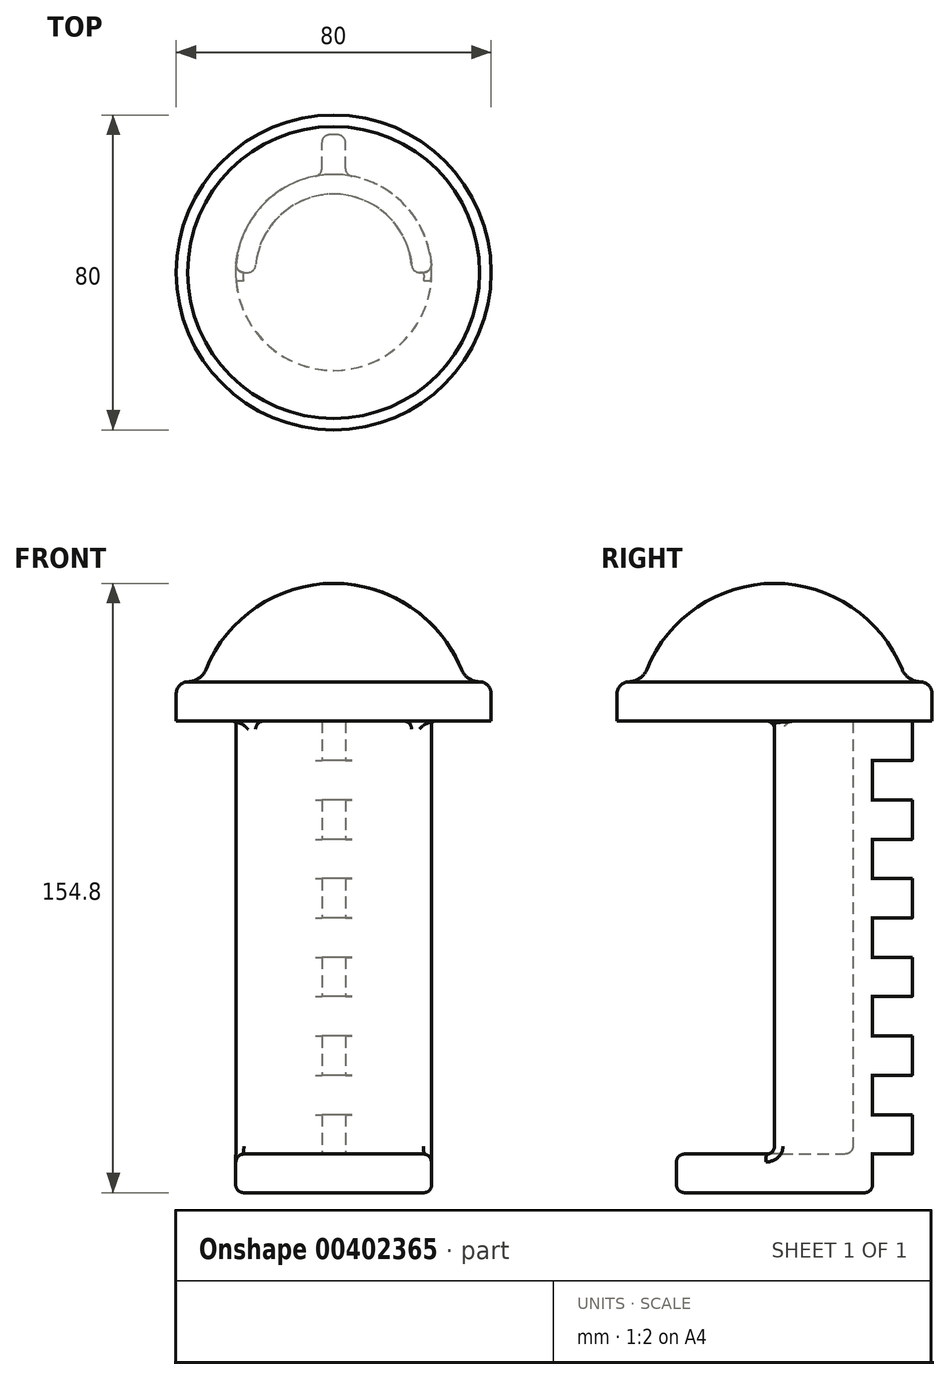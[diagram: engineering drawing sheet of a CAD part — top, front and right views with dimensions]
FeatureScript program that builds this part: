
annotation { "Feature Type Name" : "Feature", "Feature Type Description" : "" }
export const myFeature = defineFeature(function(context is Context, id is Id, definition is map)
    precondition{}
    {
        {
            var Q0;
            Q0=qCreatedBy(makeId("Top.planeOp"),FACE);
            var sketch = newSketch(context, id + "F0", { "sketchPlane" : qUnion([Q0])});
            skCircle(sketch, "E0", {"center": v(0, 0) * mm, "radius": 24.9 * mm});
            skSolve(sketch);
        }
        {
            var Q0;
            Q0=makeQuery(id+"F0.imprint","IMPRINT",FACE,{"disambiguationData":[TD([[makeQuery(id+"F0.imprint","IMPRINT",EDGE,{"derivedFrom":sQuery(id+"F0.wireOp",EDGE,"E0")}),1.0]])]});
            extrude(context, id + "F1", {"entities" : qUnion([Q0]), "depth" : 9.8 * mm});
        }
        {
            var Q0;
            Q0=makeQuery(id+"F1.opExtrude","CAP_FACE",FACE,{"disambiguationData":[OSD([sQuery(id+"F0.wireOp",EDGE,"E0")])],"isStart":false});
            var sketch = newSketch(context, id + "F2", { "sketchPlane" : qUnion([Q0])});
            skArc(sketch, "E1", {"start": v(-4.63, 24.47) * mm, "mid": v(-24.8, -2.32) * mm, "end": v(0, -24.9) * mm});
            skPoint(sketch, "E1.first.point", {"position": v(-24.85, 1.59) * mm});
            skPoint(sketch, "E1.second.point", {"position": v(24.55, 4.16) * mm});
            skPoint(sketch, "E1.third.point", {"position": v(0, -24.9) * mm});
            skArc(sketch, "E2", {"start": v(1.06, 34.98) * mm, "mid": v(0, 35) * mm, "end": v(-1.06, 34.98) * mm});
            skLineSegment(sketch, "E3", {"start": v(0, 0) * mm, "end": v(0, 45.08) * mm, "construction": true});
            skLineSegment(sketch, "E4", {"start": v(-3, 26.43) * mm, "end": v(-3, 32.98) * mm});
            skLineSegment(sketch, "E5", {"start": v(3, 26.43) * mm, "end": v(3, 32.98) * mm});
            skPoint(sketch, "E6.orphan", {"position": v(-3, 0) * mm});
            skPoint(sketch, "E7.orphan", {"position": v(3, 0) * mm});
            skPoint(sketch, "E8.visualSharp", {"position": v(-3, 24.72) * mm});
            skArc(sketch, "E8.filletArc", {"start": v(-4.63, 24.47) * mm, "mid": v(-3.46, 25.16) * mm, "end": v(-3, 26.43) * mm});
            skPoint(sketch, "E9.visualSharp", {"position": v(-3, 34.87) * mm});
            skArc(sketch, "E9.filletArc", {"start": v(-1.06, 34.98) * mm, "mid": v(-2.44, 34.38) * mm, "end": v(-3, 32.98) * mm});
            skPoint(sketch, "E10.visualSharp", {"position": v(3, 34.87) * mm});
            skArc(sketch, "E10.filletArc", {"start": v(3, 32.98) * mm, "mid": v(2.44, 34.38) * mm, "end": v(1.06, 34.98) * mm});
            skPoint(sketch, "E11.visualSharp", {"position": v(3, 24.72) * mm});
            skArc(sketch, "E11.filletArc", {"start": v(3, 26.43) * mm, "mid": v(3.46, 25.16) * mm, "end": v(4.63, 24.47) * mm});
            skArc(sketch, "E12", {"start": v(19.9, 0) * mm, "mid": v(0, 19.9) * mm, "end": v(-19.9, 0) * mm});
            skLineSegment(sketch, "E13", {"start": v(-24.9, 0) * mm, "end": v(-19.9, 0) * mm});
            skLineSegment(sketch, "E14.trimOffspring", {"start": v(19.9, 0) * mm, "end": v(24.9, 0) * mm});
            skArc(sketch, "E15.trimOffspring", {"start": v(24.9, 0) * mm, "mid": v(19.17, 15.89) * mm, "end": v(4.63, 24.47) * mm});
            skSolve(sketch);
        }
        {
            var Q0;
            Q0 = qSketchRegion(id + "F2", true);
            extrude(context, id + "F3", {"entities" : qUnion([Q0]), "operationType" : NewBodyOperationType.ADD, "depth" : 10 * mm});
        }
        {
            var Q0;
            Q0=makeQuery(id+"F3.opExtrude","CAP_FACE",FACE,{"disambiguationData":[OSD([sQuery(id+"F2.wireOp",EDGE,"E1"),sQuery(id+"F2.wireOp",EDGE,"E2"),sQuery(id+"F2.wireOp",EDGE,"E4"),sQuery(id+"F2.wireOp",EDGE,"E5"),sQuery(id+"F2.wireOp",EDGE,"E8.filletArc"),sQuery(id+"F2.wireOp",EDGE,"E9.filletArc"),sQuery(id+"F2.wireOp",EDGE,"E10.filletArc"),sQuery(id+"F2.wireOp",EDGE,"E11.filletArc"),sQuery(id+"F2.wireOp",EDGE,"E12"),sQuery(id+"F2.wireOp",EDGE,"E13"),sQuery(id+"F2.wireOp",EDGE,"E14.trimOffspring"),sQuery(id+"F2.wireOp",EDGE,"E15.trimOffspring")])],"isStart":false});
            var sketch = newSketch(context, id + "F4", { "sketchPlane" : qUnion([Q0])});
            skArc(sketch, "E16", {"start": v(19.9, 0) * mm, "mid": v(0, 19.9) * mm, "end": v(-19.9, 0) * mm});
            skArc(sketch, "E17", {"start": v(24.9, 0) * mm, "mid": v(0, 24.9) * mm, "end": v(-24.9, 0) * mm});
            skLineSegment(sketch, "E18", {"start": v(24.9, 0) * mm, "end": v(19.9, 0) * mm});
            skLineSegment(sketch, "E19.trimOffspring", {"start": v(-19.9, 0) * mm, "end": v(-24.9, 0) * mm});
            skSolve(sketch);
        }
        {
            var Q0;
            Q0=makeQuery(id+"F4.imprint","IMPRINT",FACE,{"disambiguationData":[TD([[makeQuery(id+"F4.imprint","IMPRINT",EDGE,{"derivedFrom":sQuery(id+"F4.wireOp",EDGE,"E16")}),-1.0]])]});
            extrude(context, id + "F5", {"entities" : qUnion([Q0]), "operationType" : NewBodyOperationType.ADD, "depth" : 10 * mm});
        }
        {
            var Q0;
            Q0=makeQuery(id+"F5.opExtrude","CAP_FACE",FACE,{"disambiguationData":[OSD([sQuery(id+"F4.wireOp",EDGE,"E16"),sQuery(id+"F4.wireOp",EDGE,"E17"),sQuery(id+"F4.wireOp",EDGE,"E18"),sQuery(id+"F4.wireOp",EDGE,"E19.trimOffspring")])],"isStart":false});
            var sketch = newSketch(context, id + "F6", { "sketchPlane" : qUnion([Q0])});
            skArc(sketch, "E20", {"start": v(19.9, 0) * mm, "mid": v(0, 19.9) * mm, "end": v(-19.9, 0) * mm});
            skPoint(sketch, "E20.first.point", {"position": v(-18.97, 6.02) * mm});
            skPoint(sketch, "E20.second.point", {"position": v(3.48, 19.6) * mm});
            skPoint(sketch, "E20.third.point", {"position": v(17.46, 9.55) * mm});
            skArc(sketch, "E21", {"start": v(24.9, 0) * mm, "mid": v(19.17, 15.89) * mm, "end": v(4.63, 24.47) * mm});
            skLineSegment(sketch, "E22", {"start": v(24.9, 0) * mm, "end": v(19.9, 0) * mm});
            skArc(sketch, "E23", {"start": v(1.06, 34.98) * mm, "mid": v(0, 35) * mm, "end": v(-1.06, 34.98) * mm});
            skLineSegment(sketch, "E24", {"start": v(-3, 26.43) * mm, "end": v(-3, 32.98) * mm});
            skLineSegment(sketch, "E25", {"start": v(3, 26.43) * mm, "end": v(3, 32.98) * mm});
            skLineSegment(sketch, "E26", {"start": v(0, 0) * mm, "end": v(0, 56.77) * mm, "construction": true});
            skLineSegment(sketch, "E27.trimOffspring", {"start": v(-19.9, 0) * mm, "end": v(-24.9, 0) * mm});
            skArc(sketch, "E28.trimOffspring", {"start": v(-4.63, 24.47) * mm, "mid": v(-19.17, 15.89) * mm, "end": v(-24.9, 0) * mm});
            skArc(sketch, "E29.filletArc", {"start": v(3, 26.43) * mm, "mid": v(3.46, 25.16) * mm, "end": v(4.63, 24.47) * mm});
            skPoint(sketch, "E30.visualSharp", {"position": v(3, 34.87) * mm});
            skArc(sketch, "E30.filletArc", {"start": v(3, 32.98) * mm, "mid": v(2.44, 34.38) * mm, "end": v(1.06, 34.98) * mm});
            skPoint(sketch, "E31.visualSharp", {"position": v(-3, 34.87) * mm});
            skArc(sketch, "E31.filletArc", {"start": v(-1.06, 34.98) * mm, "mid": v(-2.44, 34.38) * mm, "end": v(-3, 32.98) * mm});
            skArc(sketch, "E32.filletArc", {"start": v(-4.63, 24.47) * mm, "mid": v(-3.46, 25.16) * mm, "end": v(-3, 26.43) * mm});
            skSolve(sketch);
        }
        {
            var Q0;
            Q0 = qSketchRegion(id + "F6", true);
            extrude(context, id + "F7", {"entities" : qUnion([Q0]), "operationType" : NewBodyOperationType.ADD, "depth" : 10 * mm});
        }
        {
            var Q0;
            Q0=makeQuery(id+"F7.opExtrude","CAP_FACE",FACE,{"disambiguationData":[OSD([sQuery(id+"F6.wireOp",EDGE,"E20"),sQuery(id+"F6.wireOp",EDGE,"E21"),sQuery(id+"F6.wireOp",EDGE,"E22"),sQuery(id+"F6.wireOp",EDGE,"E23"),sQuery(id+"F6.wireOp",EDGE,"E24"),sQuery(id+"F6.wireOp",EDGE,"E25"),sQuery(id+"F6.wireOp",EDGE,"E27.trimOffspring"),sQuery(id+"F6.wireOp",EDGE,"E28.trimOffspring"),sQuery(id+"F6.wireOp",EDGE,"E29.filletArc"),sQuery(id+"F6.wireOp",EDGE,"E30.filletArc"),sQuery(id+"F6.wireOp",EDGE,"E31.filletArc"),sQuery(id+"F6.wireOp",EDGE,"E32.filletArc")])],"isStart":false});
            var sketch = newSketch(context, id + "F8", { "sketchPlane" : qUnion([Q0])});
            skArc(sketch, "E33", {"start": v(19.9, 0) * mm, "mid": v(0, 19.9) * mm, "end": v(-19.9, 0) * mm});
            skPoint(sketch, "E33.first.point", {"position": v(-19.37, 4.56) * mm});
            skPoint(sketch, "E33.second.point", {"position": v(0, 19.9) * mm});
            skPoint(sketch, "E33.third.point", {"position": v(12.83, 15.21) * mm});
            skArc(sketch, "E34", {"start": v(24.9, 0) * mm, "mid": v(0, 24.9) * mm, "end": v(-24.9, 0) * mm});
            skLineSegment(sketch, "E35", {"start": v(-24.9, 0) * mm, "end": v(-19.9, 0) * mm});
            skLineSegment(sketch, "E36.trimOffspring", {"start": v(19.9, 0) * mm, "end": v(24.9, 0) * mm});
            skSolve(sketch);
        }
        {
            var Q0;
            Q0=makeQuery(id+"F8.imprint","IMPRINT",FACE,{"disambiguationData":[TD([[makeQuery(id+"F8.imprint","IMPRINT",EDGE,{"derivedFrom":sQuery(id+"F8.wireOp",EDGE,"E33")}),-1.0]])]});
            extrude(context, id + "F9", {"entities" : qUnion([Q0]), "operationType" : NewBodyOperationType.ADD, "depth" : 10 * mm});
        }
        {
            var Q0;
            Q0=makeQuery(id+"F9.opExtrude","CAP_FACE",FACE,{"disambiguationData":[OSD([sQuery(id+"F8.wireOp",EDGE,"E33"),sQuery(id+"F8.wireOp",EDGE,"E34"),sQuery(id+"F8.wireOp",EDGE,"E35"),sQuery(id+"F8.wireOp",EDGE,"E36.trimOffspring")])],"isStart":false});
            var sketch = newSketch(context, id + "F10", { "sketchPlane" : qUnion([Q0])});
            skArc(sketch, "E37", {"start": v(19.9, 0) * mm, "mid": v(0, 19.9) * mm, "end": v(-19.9, 0) * mm});
            skPoint(sketch, "E37.first.point", {"position": v(-19.75, 2.44) * mm});
            skPoint(sketch, "E37.second.point", {"position": v(-1.95, 19.8) * mm});
            skPoint(sketch, "E37.third.point", {"position": v(19.22, 5.17) * mm});
            skArc(sketch, "E38", {"start": v(24.9, 0) * mm, "mid": v(19.17, 15.89) * mm, "end": v(4.63, 24.47) * mm});
            skPoint(sketch, "E38.first.point", {"position": v(-19.14, 15.92) * mm});
            skPoint(sketch, "E38.second.point", {"position": v(8.15, 23.53) * mm});
            skPoint(sketch, "E38.third.point", {"position": v(24.48, 4.54) * mm});
            skArc(sketch, "E39", {"start": v(1.06, 34.98) * mm, "mid": v(0, 35) * mm, "end": v(-1.06, 34.98) * mm});
            skLineSegment(sketch, "E40", {"start": v(24.9, 0) * mm, "end": v(19.9, 0) * mm});
            skLineSegment(sketch, "E41", {"start": v(0, 0) * mm, "end": v(0, 39.15) * mm, "construction": true});
            skLineSegment(sketch, "E42", {"start": v(-3, 26.43) * mm, "end": v(-3, 32.98) * mm});
            skLineSegment(sketch, "E43", {"start": v(3, 26.43) * mm, "end": v(3, 32.98) * mm});
            skArc(sketch, "E44.trimOffspring", {"start": v(-4.63, 24.47) * mm, "mid": v(-19.17, 15.89) * mm, "end": v(-24.9, 0) * mm});
            skLineSegment(sketch, "E45.trimOffspring", {"start": v(-19.9, 0) * mm, "end": v(-24.9, 0) * mm});
            skPoint(sketch, "E46.visualSharp", {"position": v(-3, 24.72) * mm});
            skArc(sketch, "E46.filletArc", {"start": v(-4.63, 24.47) * mm, "mid": v(-3.46, 25.16) * mm, "end": v(-3, 26.43) * mm});
            skPoint(sketch, "E47.visualSharp", {"position": v(3, 24.72) * mm});
            skArc(sketch, "E47.filletArc", {"start": v(3, 26.43) * mm, "mid": v(3.46, 25.16) * mm, "end": v(4.63, 24.47) * mm});
            skPoint(sketch, "E48.visualSharp", {"position": v(-3, 34.87) * mm});
            skArc(sketch, "E48.filletArc", {"start": v(-1.06, 34.98) * mm, "mid": v(-2.44, 34.38) * mm, "end": v(-3, 32.98) * mm});
            skPoint(sketch, "E49.visualSharp", {"position": v(3, 34.87) * mm});
            skArc(sketch, "E49.filletArc", {"start": v(3, 32.98) * mm, "mid": v(2.44, 34.38) * mm, "end": v(1.06, 34.98) * mm});
            skSolve(sketch);
        }
        {
            var Q0;
            Q0 = qSketchRegion(id + "F10", true);
            extrude(context, id + "F11", {"entities" : qUnion([Q0]), "operationType" : NewBodyOperationType.ADD, "depth" : 10 * mm});
        }
        {
            var Q0;
            Q0=makeQuery(id+"F11.opExtrude","CAP_FACE",FACE,{"disambiguationData":[OSD([sQuery(id+"F10.wireOp",EDGE,"E37"),sQuery(id+"F10.wireOp",EDGE,"E38"),sQuery(id+"F10.wireOp",EDGE,"E39"),sQuery(id+"F10.wireOp",EDGE,"E40"),sQuery(id+"F10.wireOp",EDGE,"E42"),sQuery(id+"F10.wireOp",EDGE,"E43"),sQuery(id+"F10.wireOp",EDGE,"E44.trimOffspring"),sQuery(id+"F10.wireOp",EDGE,"E45.trimOffspring"),sQuery(id+"F10.wireOp",EDGE,"E46.filletArc"),sQuery(id+"F10.wireOp",EDGE,"E47.filletArc"),sQuery(id+"F10.wireOp",EDGE,"E48.filletArc"),sQuery(id+"F10.wireOp",EDGE,"E49.filletArc")])],"isStart":false});
            var sketch = newSketch(context, id + "F12", { "sketchPlane" : qUnion([Q0])});
            skArc(sketch, "E50", {"start": v(19.9, 0) * mm, "mid": v(0, 19.9) * mm, "end": v(-19.9, 0) * mm});
            skPoint(sketch, "E50.first.point", {"position": v(-19.35, 4.65) * mm});
            skPoint(sketch, "E50.second.point", {"position": v(-7.36, 18.49) * mm});
            skPoint(sketch, "E50.third.point", {"position": v(18.26, 7.9) * mm});
            skArc(sketch, "E51", {"start": v(24.9, 0) * mm, "mid": v(0, 24.9) * mm, "end": v(-24.9, 0) * mm});
            skLineSegment(sketch, "E52", {"start": v(-24.9, 0) * mm, "end": v(-19.9, 0) * mm});
            skLineSegment(sketch, "E53.trimOffspring", {"start": v(19.9, 0) * mm, "end": v(24.9, 0) * mm});
            skSolve(sketch);
        }
        {
            var Q0;
            Q0 = qSketchRegion(id + "F12", true);
            extrude(context, id + "F13", {"entities" : qUnion([Q0]), "operationType" : NewBodyOperationType.ADD, "depth" : 10 * mm});
        }
        {
            var Q0;
            Q0=makeQuery(id+"F13.opExtrude","CAP_FACE",FACE,{"disambiguationData":[OSD([sQuery(id+"F12.wireOp",EDGE,"E50"),sQuery(id+"F12.wireOp",EDGE,"E51"),sQuery(id+"F12.wireOp",EDGE,"E52"),sQuery(id+"F12.wireOp",EDGE,"E53.trimOffspring")])],"isStart":false});
            var sketch = newSketch(context, id + "F14", { "sketchPlane" : qUnion([Q0])});
            skArc(sketch, "E54", {"start": v(19.9, 0) * mm, "mid": v(0, 19.9) * mm, "end": v(-19.9, 0) * mm});
            skPoint(sketch, "E54.first.point", {"position": v(16.62, 10.94) * mm});
            skPoint(sketch, "E54.second.point", {"position": v(3.42, 19.6) * mm});
            skPoint(sketch, "E54.third.point", {"position": v(-17.92, 8.65) * mm});
            skArc(sketch, "E55", {"start": v(24.9, 0) * mm, "mid": v(19.17, 15.89) * mm, "end": v(4.63, 24.47) * mm});
            skArc(sketch, "E56", {"start": v(1.06, 34.98) * mm, "mid": v(0, 35) * mm, "end": v(-1.06, 34.98) * mm});
            skLineSegment(sketch, "E57", {"start": v(-24.9, 0) * mm, "end": v(-19.9, 0) * mm});
            skLineSegment(sketch, "E58", {"start": v(0, 0) * mm, "end": v(0, 36.44) * mm, "construction": true});
            skLineSegment(sketch, "E59", {"start": v(-3, 26.43) * mm, "end": v(-3, 32.98) * mm});
            skLineSegment(sketch, "E60", {"start": v(3, 26.43) * mm, "end": v(3, 32.98) * mm});
            skArc(sketch, "E61.trimOffspring", {"start": v(-4.63, 24.47) * mm, "mid": v(-19.17, 15.89) * mm, "end": v(-24.9, 0) * mm});
            skLineSegment(sketch, "E62.trimOffspring", {"start": v(19.9, 0) * mm, "end": v(24.9, 0) * mm});
            skPoint(sketch, "E63.visualSharp", {"position": v(-3, 24.72) * mm});
            skArc(sketch, "E63.filletArc", {"start": v(-4.63, 24.47) * mm, "mid": v(-3.46, 25.16) * mm, "end": v(-3, 26.43) * mm});
            skPoint(sketch, "E64.visualSharp", {"position": v(-3, 34.87) * mm});
            skArc(sketch, "E64.filletArc", {"start": v(-1.06, 34.98) * mm, "mid": v(-2.44, 34.38) * mm, "end": v(-3, 32.98) * mm});
            skPoint(sketch, "E65.visualSharp", {"position": v(3, 34.87) * mm});
            skArc(sketch, "E65.filletArc", {"start": v(3, 32.98) * mm, "mid": v(2.44, 34.38) * mm, "end": v(1.06, 34.98) * mm});
            skPoint(sketch, "E66.visualSharp", {"position": v(3, 24.72) * mm});
            skArc(sketch, "E66.filletArc", {"start": v(3, 26.43) * mm, "mid": v(3.46, 25.16) * mm, "end": v(4.63, 24.47) * mm});
            skSolve(sketch);
        }
        {
            var Q0;
            Q0 = qSketchRegion(id + "F14", true);
            extrude(context, id + "F15", {"entities" : qUnion([Q0]), "operationType" : NewBodyOperationType.ADD, "depth" : 10 * mm});
        }
        {
            var Q0;
            Q0=makeQuery(id+"F15.opExtrude","CAP_FACE",FACE,{"disambiguationData":[OSD([sQuery(id+"F14.wireOp",EDGE,"E54"),sQuery(id+"F14.wireOp",EDGE,"E55"),sQuery(id+"F14.wireOp",EDGE,"E56"),sQuery(id+"F14.wireOp",EDGE,"E57"),sQuery(id+"F14.wireOp",EDGE,"E59"),sQuery(id+"F14.wireOp",EDGE,"E60"),sQuery(id+"F14.wireOp",EDGE,"E61.trimOffspring"),sQuery(id+"F14.wireOp",EDGE,"E62.trimOffspring"),sQuery(id+"F14.wireOp",EDGE,"E63.filletArc"),sQuery(id+"F14.wireOp",EDGE,"E64.filletArc"),sQuery(id+"F14.wireOp",EDGE,"E65.filletArc"),sQuery(id+"F14.wireOp",EDGE,"E66.filletArc")])],"isStart":false});
            var sketch = newSketch(context, id + "F16", { "sketchPlane" : qUnion([Q0])});
            skArc(sketch, "E67", {"start": v(19.9, 0) * mm, "mid": v(0, 19.9) * mm, "end": v(-19.9, 0) * mm});
            skPoint(sketch, "E67.first.point", {"position": v(-19.61, 3.37) * mm});
            skPoint(sketch, "E67.second.point", {"position": v(-4.07, 19.48) * mm});
            skPoint(sketch, "E67.third.point", {"position": v(18.8, 6.54) * mm});
            skArc(sketch, "E68", {"start": v(24.9, 0) * mm, "mid": v(0, 24.9) * mm, "end": v(-24.9, 0) * mm});
            skLineSegment(sketch, "E69", {"start": v(-24.9, 0) * mm, "end": v(-19.9, 0) * mm});
            skLineSegment(sketch, "E70.trimOffspring", {"start": v(19.9, 0) * mm, "end": v(24.9, 0) * mm});
            skSolve(sketch);
        }
        {
            var Q0;
            Q0 = qSketchRegion(id + "F16", true);
            extrude(context, id + "F17", {"entities" : qUnion([Q0]), "operationType" : NewBodyOperationType.ADD, "depth" : 10 * mm});
        }
        {
            var Q0;
            Q0=makeQuery(id+"F17.opExtrude","CAP_FACE",FACE,{"disambiguationData":[OSD([sQuery(id+"F16.wireOp",EDGE,"E67"),sQuery(id+"F16.wireOp",EDGE,"E68"),sQuery(id+"F16.wireOp",EDGE,"E69"),sQuery(id+"F16.wireOp",EDGE,"E70.trimOffspring")])],"isStart":false});
            var sketch = newSketch(context, id + "F18", { "sketchPlane" : qUnion([Q0])});
            skArc(sketch, "E71", {"start": v(19.9, 0) * mm, "mid": v(0, 19.9) * mm, "end": v(-19.9, 0) * mm});
            skPoint(sketch, "E71.first.point", {"position": v(-19.39, 4.5) * mm});
            skPoint(sketch, "E71.second.point", {"position": v(-4.82, 19.3) * mm});
            skPoint(sketch, "E71.third.point", {"position": v(18.4, 7.6) * mm});
            skArc(sketch, "E72", {"start": v(-4.63, 24.47) * mm, "mid": v(-19.17, 15.89) * mm, "end": v(-24.9, 0) * mm});
            skArc(sketch, "E73", {"start": v(1.06, 34.98) * mm, "mid": v(0, 35) * mm, "end": v(-1.06, 34.98) * mm});
            skLineSegment(sketch, "E74", {"start": v(24.9, 0) * mm, "end": v(19.9, 0) * mm});
            skLineSegment(sketch, "E75", {"start": v(0, 0) * mm, "end": v(0, 36.8) * mm, "construction": true});
            skLineSegment(sketch, "E76.trimOffspring", {"start": v(3, 26.43) * mm, "end": v(3, 32.98) * mm});
            skLineSegment(sketch, "E77.trimOffspring", {"start": v(-3, 26.43) * mm, "end": v(-3, 32.98) * mm});
            skLineSegment(sketch, "E78.trimOffspring", {"start": v(-19.9, 0) * mm, "end": v(-24.9, 0) * mm});
            skArc(sketch, "E79.trimOffspring", {"start": v(24.9, 0) * mm, "mid": v(19.17, 15.89) * mm, "end": v(4.63, 24.47) * mm});
            skPoint(sketch, "E80.visualSharp", {"position": v(-3, 24.72) * mm});
            skArc(sketch, "E80.filletArc", {"start": v(-4.63, 24.47) * mm, "mid": v(-3.46, 25.16) * mm, "end": v(-3, 26.43) * mm});
            skPoint(sketch, "E81.visualSharp", {"position": v(-3, 34.87) * mm});
            skArc(sketch, "E81.filletArc", {"start": v(-1.06, 34.98) * mm, "mid": v(-2.44, 34.38) * mm, "end": v(-3, 32.98) * mm});
            skPoint(sketch, "E82.visualSharp", {"position": v(3, 34.87) * mm});
            skArc(sketch, "E82.filletArc", {"start": v(3, 32.98) * mm, "mid": v(2.44, 34.38) * mm, "end": v(1.06, 34.98) * mm});
            skPoint(sketch, "E83.visualSharp", {"position": v(3, 24.72) * mm});
            skArc(sketch, "E83.filletArc", {"start": v(3, 26.43) * mm, "mid": v(3.46, 25.16) * mm, "end": v(4.63, 24.47) * mm});
            skSolve(sketch);
        }
        {
            var Q0;
            Q0 = qSketchRegion(id + "F18", true);
            extrude(context, id + "F19", {"entities" : qUnion([Q0]), "operationType" : NewBodyOperationType.ADD, "depth" : 10 * mm});
        }
        {
            var Q0;
            Q0=makeQuery(id+"F19.opExtrude","CAP_FACE",FACE,{"disambiguationData":[OSD([sQuery(id+"F18.wireOp",EDGE,"E71"),sQuery(id+"F18.wireOp",EDGE,"E72"),sQuery(id+"F18.wireOp",EDGE,"E73"),sQuery(id+"F18.wireOp",EDGE,"E74"),sQuery(id+"F18.wireOp",EDGE,"E76.trimOffspring"),sQuery(id+"F18.wireOp",EDGE,"E77.trimOffspring"),sQuery(id+"F18.wireOp",EDGE,"E78.trimOffspring"),sQuery(id+"F18.wireOp",EDGE,"E79.trimOffspring"),sQuery(id+"F18.wireOp",EDGE,"E80.filletArc"),sQuery(id+"F18.wireOp",EDGE,"E81.filletArc"),sQuery(id+"F18.wireOp",EDGE,"E82.filletArc"),sQuery(id+"F18.wireOp",EDGE,"E83.filletArc")])],"isStart":false});
            var sketch = newSketch(context, id + "F20", { "sketchPlane" : qUnion([Q0])});
            skArc(sketch, "E84", {"start": v(19.9, 0) * mm, "mid": v(0, 19.9) * mm, "end": v(-19.9, 0) * mm});
            skPoint(sketch, "E84.first.point", {"position": v(19.63, 3.26) * mm});
            skPoint(sketch, "E84.second.point", {"position": v(2.87, 19.7) * mm});
            skPoint(sketch, "E84.third.point", {"position": v(-18.21, 8.02) * mm});
            skArc(sketch, "E85", {"start": v(24.9, 0) * mm, "mid": v(0, 24.9) * mm, "end": v(-24.9, 0) * mm});
            skLineSegment(sketch, "E86", {"start": v(24.9, 0) * mm, "end": v(19.9, 0) * mm});
            skLineSegment(sketch, "E87.trimOffspring", {"start": v(-19.9, 0) * mm, "end": v(-24.9, 0) * mm});
            skSolve(sketch);
        }
        {
            var Q0;
            Q0 = qSketchRegion(id + "F20", true);
            extrude(context, id + "F21", {"entities" : qUnion([Q0]), "operationType" : NewBodyOperationType.ADD, "depth" : 10 * mm});
        }
        {
            var Q0;
            Q0=makeQuery(id+"F21.opExtrude","CAP_FACE",FACE,{"disambiguationData":[OSD([sQuery(id+"F20.wireOp",EDGE,"E84"),sQuery(id+"F20.wireOp",EDGE,"E85"),sQuery(id+"F20.wireOp",EDGE,"E86"),sQuery(id+"F20.wireOp",EDGE,"E87.trimOffspring")])],"isStart":false});
            var sketch = newSketch(context, id + "F22", { "sketchPlane" : qUnion([Q0])});
            skArc(sketch, "E88", {"start": v(19.9, 0) * mm, "mid": v(0, 19.9) * mm, "end": v(-19.9, 0) * mm});
            skPoint(sketch, "E88.first.point", {"position": v(19.38, 4.53) * mm});
            skPoint(sketch, "E88.second.point", {"position": v(-1.9, 19.8) * mm});
            skPoint(sketch, "E88.third.point", {"position": v(-19.57, 3.59) * mm});
            skArc(sketch, "E89", {"start": v(24.9, 0) * mm, "mid": v(19.17, 15.89) * mm, "end": v(4.63, 24.47) * mm});
            skArc(sketch, "E90", {"start": v(1.06, 34.98) * mm, "mid": v(0, 35) * mm, "end": v(-1.06, 34.98) * mm});
            skLineSegment(sketch, "E91", {"start": v(24.9, 0) * mm, "end": v(19.9, 0) * mm});
            skLineSegment(sketch, "E92", {"start": v(0, 0) * mm, "end": v(0, 49.07) * mm, "construction": true});
            skLineSegment(sketch, "E93.trimOffspring", {"start": v(3, 26.43) * mm, "end": v(3, 32.98) * mm});
            skLineSegment(sketch, "E94.trimOffspring", {"start": v(-3, 26.43) * mm, "end": v(-3, 32.98) * mm});
            skLineSegment(sketch, "E95.trimOffspring", {"start": v(-19.9, 0) * mm, "end": v(-24.9, 0) * mm});
            skArc(sketch, "E96.trimOffspring", {"start": v(-4.63, 24.47) * mm, "mid": v(-19.17, 15.89) * mm, "end": v(-24.9, 0) * mm});
            skPoint(sketch, "E97.visualSharp", {"position": v(3, 24.72) * mm});
            skArc(sketch, "E97.filletArc", {"start": v(3, 26.43) * mm, "mid": v(3.46, 25.16) * mm, "end": v(4.63, 24.47) * mm});
            skPoint(sketch, "E98.visualSharp", {"position": v(-3, 24.72) * mm});
            skArc(sketch, "E98.filletArc", {"start": v(-4.63, 24.47) * mm, "mid": v(-3.46, 25.16) * mm, "end": v(-3, 26.43) * mm});
            skPoint(sketch, "E99.visualSharp", {"position": v(-3, 34.87) * mm});
            skArc(sketch, "E99.filletArc", {"start": v(-1.06, 34.98) * mm, "mid": v(-2.44, 34.38) * mm, "end": v(-3, 32.98) * mm});
            skPoint(sketch, "E100.visualSharp", {"position": v(3, 34.87) * mm});
            skArc(sketch, "E100.filletArc", {"start": v(3, 32.98) * mm, "mid": v(2.44, 34.38) * mm, "end": v(1.06, 34.98) * mm});
            skSolve(sketch);
        }
        {
            var Q0;
            Q0 = qSketchRegion(id + "F22", true);
            extrude(context, id + "F23", {"entities" : qUnion([Q0]), "operationType" : NewBodyOperationType.ADD, "depth" : 10 * mm});
        }
        {
            var Q0;
            Q0=qCreatedBy(makeId("Front.planeOp"),FACE);
            var sketch = newSketch(context, id + "F24", { "sketchPlane" : qUnion([Q0])});
            skLineSegment(sketch, "E101", {"start": v(0, 0) * mm, "end": v(0, 164.04) * mm, "construction": true});
            skPoint(sketch, "E102", {"position": v(0, 119.8) * mm});
            skLineSegment(sketch, "E103", {"start": v(0, 119.8) * mm, "end": v(40, 119.8) * mm});
            skLineSegment(sketch, "E104", {"start": v(40, 119.8) * mm, "end": v(40, 126.8) * mm});
            skLineSegment(sketch, "E105", {"start": v(37.08, 129.8) * mm, "end": v(37, 129.8) * mm});
            skArc(sketch, "E106", {"start": v(32.45, 132.92) * mm, "mid": v(19.57, 148.82) * mm, "end": v(0, 154.8) * mm});
            skPoint(sketch, "E107.visualSharp", {"position": v(33.54, 129.8) * mm});
            skArc(sketch, "E107.filletArc", {"start": v(32.45, 132.92) * mm, "mid": v(34.29, 130.65) * mm, "end": v(37.08, 129.8) * mm});
            skPoint(sketch, "E108.visualSharp", {"position": v(40, 129.8) * mm});
            skArc(sketch, "E108.filletArc", {"start": v(40, 126.8) * mm, "mid": v(39.12, 128.92) * mm, "end": v(37, 129.8) * mm});
            skLineSegment(sketch, "E109", {"start": v(0, 154.8) * mm, "end": v(0, 119.8) * mm});
            skSolve(sketch);
        }
        {
            var Q0;
            Q0=makeQuery(id+"F24.imprint","IMPRINT",FACE,{"disambiguationData":[TD([[makeQuery(id+"F24.imprint","IMPRINT",EDGE,{"derivedFrom":sQuery(id+"F24.wireOp",EDGE,"E103")}),1.0]])]});
            var Q1;
            Q1=sQuery(id+"F24.wireOp",EDGE,"E101");
            revolve(context, id + "F25", {"operationType" : NewBodyOperationType.ADD, "entities" : qUnion([Q0]), "axis" : qUnion([Q1]), "revolveType" : RevolveType.FULL});
        }
        {
            var Q0;
            Q0=makeQuery(id+"F23.boolean.opBoolean","MERGE",EDGE,{"derivedFrom":[makeQuery(id+"F21.boolean.opBoolean","MERGE",EDGE,{"derivedFrom":[makeQuery(id+"F19.boolean.opBoolean","MERGE",EDGE,{"derivedFrom":[makeQuery(id+"F17.boolean.opBoolean","MERGE",EDGE,{"derivedFrom":[makeQuery(id+"F15.boolean.opBoolean","MERGE",EDGE,{"derivedFrom":[makeQuery(id+"F13.boolean.opBoolean","MERGE",EDGE,{"derivedFrom":[makeQuery(id+"F11.boolean.opBoolean","MERGE",EDGE,{"derivedFrom":[makeQuery(id+"F9.boolean.opBoolean","MERGE",EDGE,{"derivedFrom":[makeQuery(id+"F7.boolean.opBoolean","MERGE",EDGE,{"derivedFrom":[makeQuery(id+"F5.boolean.opBoolean","MERGE",EDGE,{"derivedFrom":[makeQuery(id+"F3.opExtrude","SWEPT_EDGE",EDGE,{"disambiguationData":[OSD([sQuery(id+"F2.wireOp",EDGE,"E12"),sQuery(id+"F2.wireOp",EDGE,"E13")])]}),makeQuery(id+"F5.opExtrude","SWEPT_EDGE",EDGE,{"disambiguationData":[OSD([sQuery(id+"F4.wireOp",EDGE,"E16"),sQuery(id+"F4.wireOp",EDGE,"E19.trimOffspring")])]})]}),makeQuery(id+"F7.opExtrude","SWEPT_EDGE",EDGE,{"disambiguationData":[OSD([sQuery(id+"F6.wireOp",EDGE,"E20"),sQuery(id+"F6.wireOp",EDGE,"E27.trimOffspring")])]})]}),makeQuery(id+"F9.opExtrude","SWEPT_EDGE",EDGE,{"disambiguationData":[OSD([sQuery(id+"F8.wireOp",EDGE,"E33"),sQuery(id+"F8.wireOp",EDGE,"E35")])]})]}),makeQuery(id+"F11.opExtrude","SWEPT_EDGE",EDGE,{"disambiguationData":[OSD([sQuery(id+"F10.wireOp",EDGE,"E37"),sQuery(id+"F10.wireOp",EDGE,"E45.trimOffspring")])]})]}),makeQuery(id+"F13.opExtrude","SWEPT_EDGE",EDGE,{"disambiguationData":[OSD([sQuery(id+"F12.wireOp",EDGE,"E50"),sQuery(id+"F12.wireOp",EDGE,"E52")])]})]}),makeQuery(id+"F15.opExtrude","SWEPT_EDGE",EDGE,{"disambiguationData":[OSD([sQuery(id+"F14.wireOp",EDGE,"E54"),sQuery(id+"F14.wireOp",EDGE,"E57")])]})]}),makeQuery(id+"F17.opExtrude","SWEPT_EDGE",EDGE,{"disambiguationData":[OSD([sQuery(id+"F16.wireOp",EDGE,"E67"),sQuery(id+"F16.wireOp",EDGE,"E69")])]})]}),makeQuery(id+"F19.opExtrude","SWEPT_EDGE",EDGE,{"disambiguationData":[OSD([sQuery(id+"F18.wireOp",EDGE,"E71"),sQuery(id+"F18.wireOp",EDGE,"E78.trimOffspring")])]})]}),makeQuery(id+"F21.opExtrude","SWEPT_EDGE",EDGE,{"disambiguationData":[OSD([sQuery(id+"F20.wireOp",EDGE,"E84"),sQuery(id+"F20.wireOp",EDGE,"E87.trimOffspring")])]})]}),makeQuery(id+"F23.opExtrude","SWEPT_EDGE",EDGE,{"disambiguationData":[OSD([sQuery(id+"F22.wireOp",EDGE,"E88"),sQuery(id+"F22.wireOp",EDGE,"E95.trimOffspring")])]})]});
            var Q1;
            Q1=makeQuery(id+"F23.boolean.opBoolean","MERGE",EDGE,{"derivedFrom":[makeQuery(id+"F21.boolean.opBoolean","MERGE",EDGE,{"derivedFrom":[makeQuery(id+"F19.boolean.opBoolean","MERGE",EDGE,{"derivedFrom":[makeQuery(id+"F17.boolean.opBoolean","MERGE",EDGE,{"derivedFrom":[makeQuery(id+"F15.boolean.opBoolean","MERGE",EDGE,{"derivedFrom":[makeQuery(id+"F13.boolean.opBoolean","MERGE",EDGE,{"derivedFrom":[makeQuery(id+"F11.boolean.opBoolean","MERGE",EDGE,{"derivedFrom":[makeQuery(id+"F9.boolean.opBoolean","MERGE",EDGE,{"derivedFrom":[makeQuery(id+"F7.boolean.opBoolean","MERGE",EDGE,{"derivedFrom":[makeQuery(id+"F5.boolean.opBoolean","MERGE",EDGE,{"derivedFrom":[makeQuery(id+"F3.opExtrude","SWEPT_EDGE",EDGE,{"disambiguationData":[OSD([sQuery(id+"F2.wireOp",EDGE,"E12"),sQuery(id+"F2.wireOp",EDGE,"E14.trimOffspring")])]}),makeQuery(id+"F5.opExtrude","SWEPT_EDGE",EDGE,{"disambiguationData":[OSD([sQuery(id+"F4.wireOp",EDGE,"E16"),sQuery(id+"F4.wireOp",EDGE,"E18")])]})]}),makeQuery(id+"F7.opExtrude","SWEPT_EDGE",EDGE,{"disambiguationData":[OSD([sQuery(id+"F6.wireOp",EDGE,"E20"),sQuery(id+"F6.wireOp",EDGE,"E22")])]})]}),makeQuery(id+"F9.opExtrude","SWEPT_EDGE",EDGE,{"disambiguationData":[OSD([sQuery(id+"F8.wireOp",EDGE,"E33"),sQuery(id+"F8.wireOp",EDGE,"E36.trimOffspring")])]})]}),makeQuery(id+"F11.opExtrude","SWEPT_EDGE",EDGE,{"disambiguationData":[OSD([sQuery(id+"F10.wireOp",EDGE,"E37"),sQuery(id+"F10.wireOp",EDGE,"E40")])]})]}),makeQuery(id+"F13.opExtrude","SWEPT_EDGE",EDGE,{"disambiguationData":[OSD([sQuery(id+"F12.wireOp",EDGE,"E50"),sQuery(id+"F12.wireOp",EDGE,"E53.trimOffspring")])]})]}),makeQuery(id+"F15.opExtrude","SWEPT_EDGE",EDGE,{"disambiguationData":[OSD([sQuery(id+"F14.wireOp",EDGE,"E54"),sQuery(id+"F14.wireOp",EDGE,"E62.trimOffspring")])]})]}),makeQuery(id+"F17.opExtrude","SWEPT_EDGE",EDGE,{"disambiguationData":[OSD([sQuery(id+"F16.wireOp",EDGE,"E67"),sQuery(id+"F16.wireOp",EDGE,"E70.trimOffspring")])]})]}),makeQuery(id+"F19.opExtrude","SWEPT_EDGE",EDGE,{"disambiguationData":[OSD([sQuery(id+"F18.wireOp",EDGE,"E71"),sQuery(id+"F18.wireOp",EDGE,"E74")])]})]}),makeQuery(id+"F21.opExtrude","SWEPT_EDGE",EDGE,{"disambiguationData":[OSD([sQuery(id+"F20.wireOp",EDGE,"E84"),sQuery(id+"F20.wireOp",EDGE,"E86")])]})]}),makeQuery(id+"F23.opExtrude","SWEPT_EDGE",EDGE,{"disambiguationData":[OSD([sQuery(id+"F22.wireOp",EDGE,"E88"),sQuery(id+"F22.wireOp",EDGE,"E91")])]})]});
            fillet(context, id + "F26", {"entities" : qUnion([Q0, Q1]), "radius" : 2 * mm, "tangentPropagation" : true, "allowEdgeOverflow" : false});
        }
        {
            var Q0;
            Q0=makeQuery(id+"F23.boolean.opBoolean","MERGE",EDGE,{"derivedFrom":[makeQuery(id+"F21.boolean.opBoolean","MERGE",EDGE,{"derivedFrom":[makeQuery(id+"F19.boolean.opBoolean","MERGE",EDGE,{"derivedFrom":[makeQuery(id+"F17.boolean.opBoolean","MERGE",EDGE,{"derivedFrom":[makeQuery(id+"F15.boolean.opBoolean","MERGE",EDGE,{"derivedFrom":[makeQuery(id+"F13.boolean.opBoolean","MERGE",EDGE,{"derivedFrom":[makeQuery(id+"F11.boolean.opBoolean","MERGE",EDGE,{"derivedFrom":[makeQuery(id+"F9.boolean.opBoolean","MERGE",EDGE,{"derivedFrom":[makeQuery(id+"F7.boolean.opBoolean","MERGE",EDGE,{"derivedFrom":[makeQuery(id+"F5.boolean.opBoolean","MERGE",EDGE,{"derivedFrom":[makeQuery(id+"F3.opExtrude","SWEPT_EDGE",EDGE,{"disambiguationData":[OSD([sQuery(id+"F0.wireOp",EDGE,"E0"),sQuery(id+"F2.wireOp",EDGE,"E14.trimOffspring"),sQuery(id+"F2.wireOp",EDGE,"E15.trimOffspring")])]}),makeQuery(id+"F5.opExtrude","SWEPT_EDGE",EDGE,{"disambiguationData":[OSD([sQuery(id+"F4.wireOp",EDGE,"E17"),sQuery(id+"F4.wireOp",EDGE,"E18")])]})]}),makeQuery(id+"F7.opExtrude","SWEPT_EDGE",EDGE,{"disambiguationData":[OSD([sQuery(id+"F6.wireOp",EDGE,"E21"),sQuery(id+"F6.wireOp",EDGE,"E22")])]})]}),makeQuery(id+"F9.opExtrude","SWEPT_EDGE",EDGE,{"disambiguationData":[OSD([sQuery(id+"F8.wireOp",EDGE,"E34"),sQuery(id+"F8.wireOp",EDGE,"E36.trimOffspring")])]})]}),makeQuery(id+"F11.opExtrude","SWEPT_EDGE",EDGE,{"disambiguationData":[OSD([sQuery(id+"F10.wireOp",EDGE,"E38"),sQuery(id+"F10.wireOp",EDGE,"E40")])]})]}),makeQuery(id+"F13.opExtrude","SWEPT_EDGE",EDGE,{"disambiguationData":[OSD([sQuery(id+"F12.wireOp",EDGE,"E51"),sQuery(id+"F12.wireOp",EDGE,"E53.trimOffspring")])]})]}),makeQuery(id+"F15.opExtrude","SWEPT_EDGE",EDGE,{"disambiguationData":[OSD([sQuery(id+"F14.wireOp",EDGE,"E55"),sQuery(id+"F14.wireOp",EDGE,"E62.trimOffspring")])]})]}),makeQuery(id+"F17.opExtrude","SWEPT_EDGE",EDGE,{"disambiguationData":[OSD([sQuery(id+"F16.wireOp",EDGE,"E68"),sQuery(id+"F16.wireOp",EDGE,"E70.trimOffspring")])]})]}),makeQuery(id+"F19.opExtrude","SWEPT_EDGE",EDGE,{"disambiguationData":[OSD([sQuery(id+"F18.wireOp",EDGE,"E74"),sQuery(id+"F18.wireOp",EDGE,"E79.trimOffspring")])]})]}),makeQuery(id+"F21.opExtrude","SWEPT_EDGE",EDGE,{"disambiguationData":[OSD([sQuery(id+"F20.wireOp",EDGE,"E85"),sQuery(id+"F20.wireOp",EDGE,"E86")])]})]}),makeQuery(id+"F23.opExtrude","SWEPT_EDGE",EDGE,{"disambiguationData":[OSD([sQuery(id+"F22.wireOp",EDGE,"E89"),sQuery(id+"F22.wireOp",EDGE,"E91")])]})]});
            var Q1;
            Q1=makeQuery(id+"F23.boolean.opBoolean","MERGE",EDGE,{"derivedFrom":[makeQuery(id+"F21.boolean.opBoolean","MERGE",EDGE,{"derivedFrom":[makeQuery(id+"F19.boolean.opBoolean","MERGE",EDGE,{"derivedFrom":[makeQuery(id+"F17.boolean.opBoolean","MERGE",EDGE,{"derivedFrom":[makeQuery(id+"F15.boolean.opBoolean","MERGE",EDGE,{"derivedFrom":[makeQuery(id+"F13.boolean.opBoolean","MERGE",EDGE,{"derivedFrom":[makeQuery(id+"F11.boolean.opBoolean","MERGE",EDGE,{"derivedFrom":[makeQuery(id+"F9.boolean.opBoolean","MERGE",EDGE,{"derivedFrom":[makeQuery(id+"F7.boolean.opBoolean","MERGE",EDGE,{"derivedFrom":[makeQuery(id+"F5.boolean.opBoolean","MERGE",EDGE,{"derivedFrom":[makeQuery(id+"F3.opExtrude","SWEPT_EDGE",EDGE,{"disambiguationData":[OSD([sQuery(id+"F2.wireOp",EDGE,"E1"),sQuery(id+"F2.wireOp",EDGE,"E13")])]}),makeQuery(id+"F5.opExtrude","SWEPT_EDGE",EDGE,{"disambiguationData":[OSD([sQuery(id+"F4.wireOp",EDGE,"E17"),sQuery(id+"F4.wireOp",EDGE,"E19.trimOffspring")])]})]}),makeQuery(id+"F7.opExtrude","SWEPT_EDGE",EDGE,{"disambiguationData":[OSD([sQuery(id+"F6.wireOp",EDGE,"E27.trimOffspring"),sQuery(id+"F6.wireOp",EDGE,"E28.trimOffspring")])]})]}),makeQuery(id+"F9.opExtrude","SWEPT_EDGE",EDGE,{"disambiguationData":[OSD([sQuery(id+"F8.wireOp",EDGE,"E34"),sQuery(id+"F8.wireOp",EDGE,"E35")])]})]}),makeQuery(id+"F11.opExtrude","SWEPT_EDGE",EDGE,{"disambiguationData":[OSD([sQuery(id+"F10.wireOp",EDGE,"E44.trimOffspring"),sQuery(id+"F10.wireOp",EDGE,"E45.trimOffspring")])]})]}),makeQuery(id+"F13.opExtrude","SWEPT_EDGE",EDGE,{"disambiguationData":[OSD([sQuery(id+"F12.wireOp",EDGE,"E51"),sQuery(id+"F12.wireOp",EDGE,"E52")])]})]}),makeQuery(id+"F15.opExtrude","SWEPT_EDGE",EDGE,{"disambiguationData":[OSD([sQuery(id+"F14.wireOp",EDGE,"E57"),sQuery(id+"F14.wireOp",EDGE,"E61.trimOffspring")])]})]}),makeQuery(id+"F17.opExtrude","SWEPT_EDGE",EDGE,{"disambiguationData":[OSD([sQuery(id+"F16.wireOp",EDGE,"E68"),sQuery(id+"F16.wireOp",EDGE,"E69")])]})]}),makeQuery(id+"F19.opExtrude","SWEPT_EDGE",EDGE,{"disambiguationData":[OSD([sQuery(id+"F18.wireOp",EDGE,"E72"),sQuery(id+"F18.wireOp",EDGE,"E78.trimOffspring")])]})]}),makeQuery(id+"F21.opExtrude","SWEPT_EDGE",EDGE,{"disambiguationData":[OSD([sQuery(id+"F20.wireOp",EDGE,"E85"),sQuery(id+"F20.wireOp",EDGE,"E87.trimOffspring")])]})]}),makeQuery(id+"F23.opExtrude","SWEPT_EDGE",EDGE,{"disambiguationData":[OSD([sQuery(id+"F22.wireOp",EDGE,"E95.trimOffspring"),sQuery(id+"F22.wireOp",EDGE,"E96.trimOffspring")])]})]});
            fillet(context, id + "F27", {"entities" : qUnion([Q0, Q1]), "radius" : 2 * mm, "tangentPropagation" : true, "allowEdgeOverflow" : false});
        }
        {
            var Q0;
            Q0=makeQuery(id+"F1.opExtrude","CAP_FACE",FACE,{"disambiguationData":[OSD([sQuery(id+"F0.wireOp",EDGE,"E0")])],"isStart":false});
            fillet(context, id + "F28", {"entities" : qUnion([Q0]), "radius" : 2 * mm, "tangentPropagation" : true, "allowEdgeOverflow" : false});
        }
        {
            var Q0;
            Q0=makeQuery(id+"F1.opExtrude","CAP_EDGE",EDGE,{"disambiguationData":[OSD([sQuery(id+"F0.wireOp",EDGE,"E0")])],"isStart":true});
            fillet(context, id + "F29", {"entities" : qUnion([Q0]), "radius" : 2 * mm, "tangentPropagation" : true, "allowEdgeOverflow" : false});
        }
        {
            var Q0;
            Q0=makeQuery(id+"F23.opExtrude","CAP_EDGE",EDGE,{"disambiguationData":[OSD([sQuery(id+"F22.wireOp",EDGE,"E88")])],"isStart":false});
            var Q1;
            Q1=makeQuery(id+"F26.opFillet","BLEND_EDGE",EDGE,{"blendedFrom":[makeQuery(id+"F23.boolean.opBoolean","MERGE",EDGE,{"derivedFrom":[makeQuery(id+"F21.boolean.opBoolean","MERGE",EDGE,{"derivedFrom":[makeQuery(id+"F19.boolean.opBoolean","MERGE",EDGE,{"derivedFrom":[makeQuery(id+"F17.boolean.opBoolean","MERGE",EDGE,{"derivedFrom":[makeQuery(id+"F15.boolean.opBoolean","MERGE",EDGE,{"derivedFrom":[makeQuery(id+"F13.boolean.opBoolean","MERGE",EDGE,{"derivedFrom":[makeQuery(id+"F11.boolean.opBoolean","MERGE",EDGE,{"derivedFrom":[makeQuery(id+"F9.boolean.opBoolean","MERGE",EDGE,{"derivedFrom":[makeQuery(id+"F7.boolean.opBoolean","MERGE",EDGE,{"derivedFrom":[makeQuery(id+"F5.boolean.opBoolean","MERGE",EDGE,{"derivedFrom":[makeQuery(id+"F3.opExtrude","SWEPT_EDGE",EDGE,{"disambiguationData":[OSD([sQuery(id+"F2.wireOp",EDGE,"E12"),sQuery(id+"F2.wireOp",EDGE,"E13")])]}),makeQuery(id+"F5.opExtrude","SWEPT_EDGE",EDGE,{"disambiguationData":[OSD([sQuery(id+"F4.wireOp",EDGE,"E16"),sQuery(id+"F4.wireOp",EDGE,"E19.trimOffspring")])]})]}),makeQuery(id+"F7.opExtrude","SWEPT_EDGE",EDGE,{"disambiguationData":[OSD([sQuery(id+"F6.wireOp",EDGE,"E20"),sQuery(id+"F6.wireOp",EDGE,"E27.trimOffspring")])]})]}),makeQuery(id+"F9.opExtrude","SWEPT_EDGE",EDGE,{"disambiguationData":[OSD([sQuery(id+"F8.wireOp",EDGE,"E33"),sQuery(id+"F8.wireOp",EDGE,"E35")])]})]}),makeQuery(id+"F11.opExtrude","SWEPT_EDGE",EDGE,{"disambiguationData":[OSD([sQuery(id+"F10.wireOp",EDGE,"E37"),sQuery(id+"F10.wireOp",EDGE,"E45.trimOffspring")])]})]}),makeQuery(id+"F13.opExtrude","SWEPT_EDGE",EDGE,{"disambiguationData":[OSD([sQuery(id+"F12.wireOp",EDGE,"E50"),sQuery(id+"F12.wireOp",EDGE,"E52")])]})]}),makeQuery(id+"F15.opExtrude","SWEPT_EDGE",EDGE,{"disambiguationData":[OSD([sQuery(id+"F14.wireOp",EDGE,"E54"),sQuery(id+"F14.wireOp",EDGE,"E57")])]})]}),makeQuery(id+"F17.opExtrude","SWEPT_EDGE",EDGE,{"disambiguationData":[OSD([sQuery(id+"F16.wireOp",EDGE,"E67"),sQuery(id+"F16.wireOp",EDGE,"E69")])]})]}),makeQuery(id+"F19.opExtrude","SWEPT_EDGE",EDGE,{"disambiguationData":[OSD([sQuery(id+"F18.wireOp",EDGE,"E71"),sQuery(id+"F18.wireOp",EDGE,"E78.trimOffspring")])]})]}),makeQuery(id+"F21.opExtrude","SWEPT_EDGE",EDGE,{"disambiguationData":[OSD([sQuery(id+"F20.wireOp",EDGE,"E84"),sQuery(id+"F20.wireOp",EDGE,"E87.trimOffspring")])]})]}),makeQuery(id+"F23.opExtrude","SWEPT_EDGE",EDGE,{"disambiguationData":[OSD([sQuery(id+"F22.wireOp",EDGE,"E88"),sQuery(id+"F22.wireOp",EDGE,"E95.trimOffspring")])]})]}),makeQuery(id+"F25.opRevolve","SWEPT_FACE",FACE,{"disambiguationData":[OSD([sQuery(id+"F24.wireOp",EDGE,"E103")])]})],"blendedInto":[makeQuery(id+"F25.opRevolve","SWEPT_FACE",FACE,{"disambiguationData":[OSD([sQuery(id+"F24.wireOp",EDGE,"E103")])]})]});
            var Q2;
            Q2=makeQuery(id+"F26.opFillet","BLEND_EDGE",EDGE,{"blendedFrom":[makeQuery(id+"F23.boolean.opBoolean","MERGE",EDGE,{"derivedFrom":[makeQuery(id+"F21.boolean.opBoolean","MERGE",EDGE,{"derivedFrom":[makeQuery(id+"F19.boolean.opBoolean","MERGE",EDGE,{"derivedFrom":[makeQuery(id+"F17.boolean.opBoolean","MERGE",EDGE,{"derivedFrom":[makeQuery(id+"F15.boolean.opBoolean","MERGE",EDGE,{"derivedFrom":[makeQuery(id+"F13.boolean.opBoolean","MERGE",EDGE,{"derivedFrom":[makeQuery(id+"F11.boolean.opBoolean","MERGE",EDGE,{"derivedFrom":[makeQuery(id+"F9.boolean.opBoolean","MERGE",EDGE,{"derivedFrom":[makeQuery(id+"F7.boolean.opBoolean","MERGE",EDGE,{"derivedFrom":[makeQuery(id+"F5.boolean.opBoolean","MERGE",EDGE,{"derivedFrom":[makeQuery(id+"F3.opExtrude","SWEPT_EDGE",EDGE,{"disambiguationData":[OSD([sQuery(id+"F2.wireOp",EDGE,"E12"),sQuery(id+"F2.wireOp",EDGE,"E14.trimOffspring")])]}),makeQuery(id+"F5.opExtrude","SWEPT_EDGE",EDGE,{"disambiguationData":[OSD([sQuery(id+"F4.wireOp",EDGE,"E16"),sQuery(id+"F4.wireOp",EDGE,"E18")])]})]}),makeQuery(id+"F7.opExtrude","SWEPT_EDGE",EDGE,{"disambiguationData":[OSD([sQuery(id+"F6.wireOp",EDGE,"E20"),sQuery(id+"F6.wireOp",EDGE,"E22")])]})]}),makeQuery(id+"F9.opExtrude","SWEPT_EDGE",EDGE,{"disambiguationData":[OSD([sQuery(id+"F8.wireOp",EDGE,"E33"),sQuery(id+"F8.wireOp",EDGE,"E36.trimOffspring")])]})]}),makeQuery(id+"F11.opExtrude","SWEPT_EDGE",EDGE,{"disambiguationData":[OSD([sQuery(id+"F10.wireOp",EDGE,"E37"),sQuery(id+"F10.wireOp",EDGE,"E40")])]})]}),makeQuery(id+"F13.opExtrude","SWEPT_EDGE",EDGE,{"disambiguationData":[OSD([sQuery(id+"F12.wireOp",EDGE,"E50"),sQuery(id+"F12.wireOp",EDGE,"E53.trimOffspring")])]})]}),makeQuery(id+"F15.opExtrude","SWEPT_EDGE",EDGE,{"disambiguationData":[OSD([sQuery(id+"F14.wireOp",EDGE,"E54"),sQuery(id+"F14.wireOp",EDGE,"E62.trimOffspring")])]})]}),makeQuery(id+"F17.opExtrude","SWEPT_EDGE",EDGE,{"disambiguationData":[OSD([sQuery(id+"F16.wireOp",EDGE,"E67"),sQuery(id+"F16.wireOp",EDGE,"E70.trimOffspring")])]})]}),makeQuery(id+"F19.opExtrude","SWEPT_EDGE",EDGE,{"disambiguationData":[OSD([sQuery(id+"F18.wireOp",EDGE,"E71"),sQuery(id+"F18.wireOp",EDGE,"E74")])]})]}),makeQuery(id+"F21.opExtrude","SWEPT_EDGE",EDGE,{"disambiguationData":[OSD([sQuery(id+"F20.wireOp",EDGE,"E84"),sQuery(id+"F20.wireOp",EDGE,"E86")])]})]}),makeQuery(id+"F23.opExtrude","SWEPT_EDGE",EDGE,{"disambiguationData":[OSD([sQuery(id+"F22.wireOp",EDGE,"E88"),sQuery(id+"F22.wireOp",EDGE,"E91")])]})]}),makeQuery(id+"F25.opRevolve","SWEPT_FACE",FACE,{"disambiguationData":[OSD([sQuery(id+"F24.wireOp",EDGE,"E103")])]})],"blendedInto":[makeQuery(id+"F25.opRevolve","SWEPT_FACE",FACE,{"disambiguationData":[OSD([sQuery(id+"F24.wireOp",EDGE,"E103")])]})]});
            fillet(context, id + "F30", {"entities" : qUnion([Q0, Q1, Q2]), "radius" : 2 * mm, "allowEdgeOverflow" : false});
        }
    });
